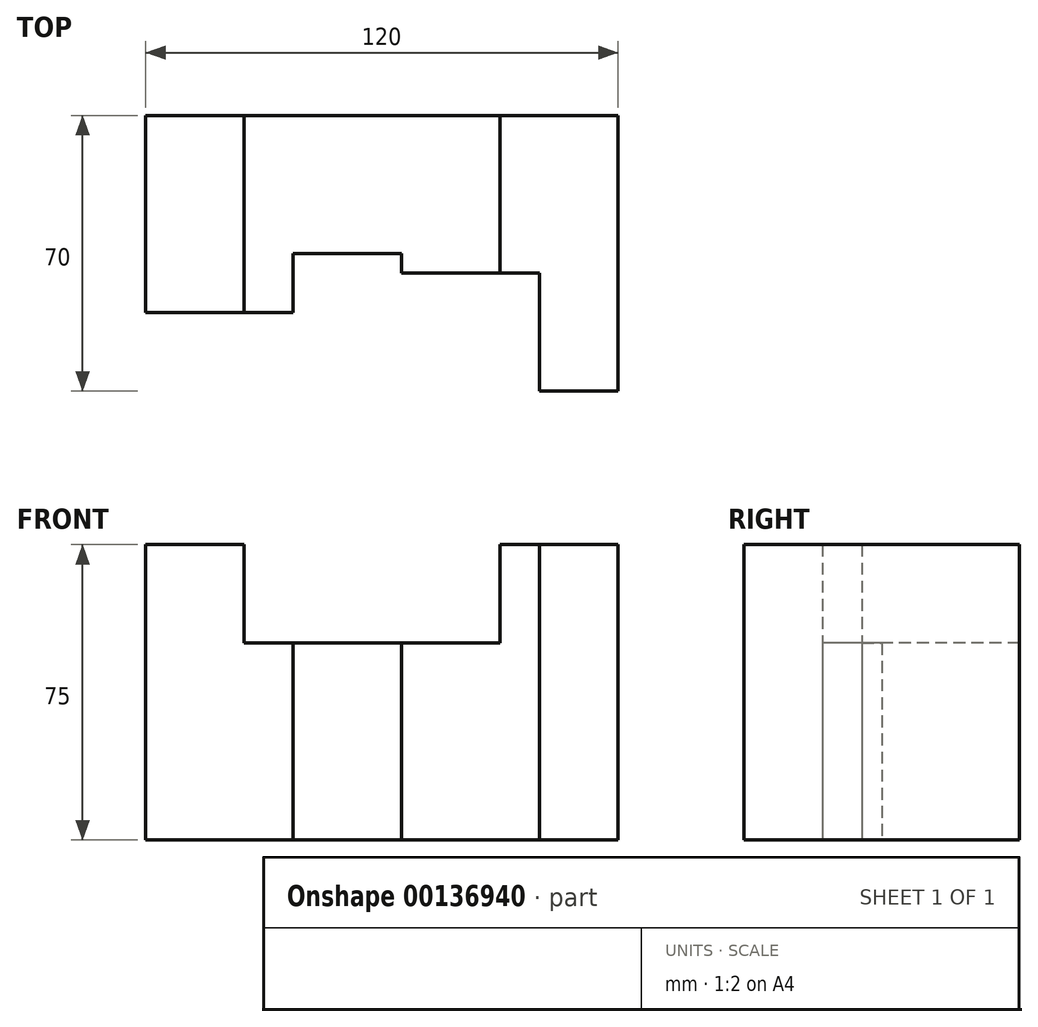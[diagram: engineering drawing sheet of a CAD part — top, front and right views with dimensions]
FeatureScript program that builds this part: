
annotation { "Feature Type Name" : "Feature", "Feature Type Description" : "" }
export const myFeature = defineFeature(function(context is Context, id is Id, definition is map)
    precondition{}
    {
        {
            var Q0;
            Q0=qCreatedBy(makeId("Top.planeOp"),FACE);
            var sketch = newSketch(context, id + "F0", { "sketchPlane" : qUnion([Q0])});
            skLineSegment(sketch, "E0", {"start": v(-37.5, 0) * mm, "end": v(27.5, 0) * mm});
            skLineSegment(sketch, "E1", {"start": v(-37.5, 0) * mm, "end": v(-37.5, -50) * mm});
            skLineSegment(sketch, "E2", {"start": v(-37.5, -50) * mm, "end": v(-62.5, -50) * mm});
            skLineSegment(sketch, "E3", {"start": v(-62.5, -50) * mm, "end": v(-62.5, 0) * mm});
            skLineSegment(sketch, "E4", {"start": v(-62.5, 0) * mm, "end": v(-37.5, 0) * mm});
            skLineSegment(sketch, "E5", {"start": v(27.5, 0) * mm, "end": v(27.5, -40) * mm});
            skLineSegment(sketch, "E6", {"start": v(27.5, -40) * mm, "end": v(37.5, -40) * mm});
            skLineSegment(sketch, "E7", {"start": v(37.5, -40) * mm, "end": v(37.5, 0) * mm});
            skLineSegment(sketch, "E8", {"start": v(37.5, 0) * mm, "end": v(27.5, 0) * mm});
            skLineSegment(sketch, "E9", {"start": v(37.5, -40) * mm, "end": v(37.5, -70) * mm});
            skLineSegment(sketch, "E10", {"start": v(37.5, -70) * mm, "end": v(57.5, -70) * mm});
            skLineSegment(sketch, "E11", {"start": v(57.5, -70) * mm, "end": v(57.5, 0) * mm});
            skLineSegment(sketch, "E12", {"start": v(57.5, 0) * mm, "end": v(37.5, 0) * mm});
            skLineSegment(sketch, "E13", {"start": v(27.5, -40) * mm, "end": v(2.5, -40) * mm});
            skLineSegment(sketch, "E14", {"start": v(2.5, -40) * mm, "end": v(2.5, -35) * mm});
            skLineSegment(sketch, "E15", {"start": v(2.5, -35) * mm, "end": v(-25, -35) * mm});
            skLineSegment(sketch, "E16", {"start": v(-25, -35) * mm, "end": v(-25, -50) * mm});
            skLineSegment(sketch, "E17", {"start": v(-25, -50) * mm, "end": v(-37.5, -50) * mm});
            skSolve(sketch);
        }
        {
            var Q0;
            Q0=makeQuery(id+"F0.imprint","IMPRINT",FACE,{"disambiguationData":[TD([[makeQuery(id+"F0.imprint","IMPRINT",EDGE,{"derivedFrom":sQuery(id+"F0.wireOp",EDGE,"E0")}),-1.0]])]});
            extrude(context, id + "F1", {"entities" : qUnion([Q0]), "depth" : 50 * mm});
        }
        {
            var Q0;
            Q0=makeQuery(id+"F0.imprint","IMPRINT",FACE,{"disambiguationData":[TD([[makeQuery(id+"F0.imprint","IMPRINT",EDGE,{"derivedFrom":sQuery(id+"F0.wireOp",EDGE,"E1")}),-1.0]])]});
            var Q1;
            Q1=makeQuery(id+"F0.imprint","IMPRINT",FACE,{"disambiguationData":[TD([[makeQuery(id+"F0.imprint","IMPRINT",EDGE,{"derivedFrom":sQuery(id+"F0.wireOp",EDGE,"E5")}),1.0]])]});
            var Q2;
            Q2=makeQuery(id+"F0.imprint","IMPRINT",FACE,{"disambiguationData":[TD([[makeQuery(id+"F0.imprint","IMPRINT",EDGE,{"derivedFrom":sQuery(id+"F0.wireOp",EDGE,"E7")}),-1.0]])]});
            extrude(context, id + "F2", {"entities" : qUnion([Q0, Q1, Q2]), "operationType" : NewBodyOperationType.ADD, "depth" : 75 * mm});
        }
    });
